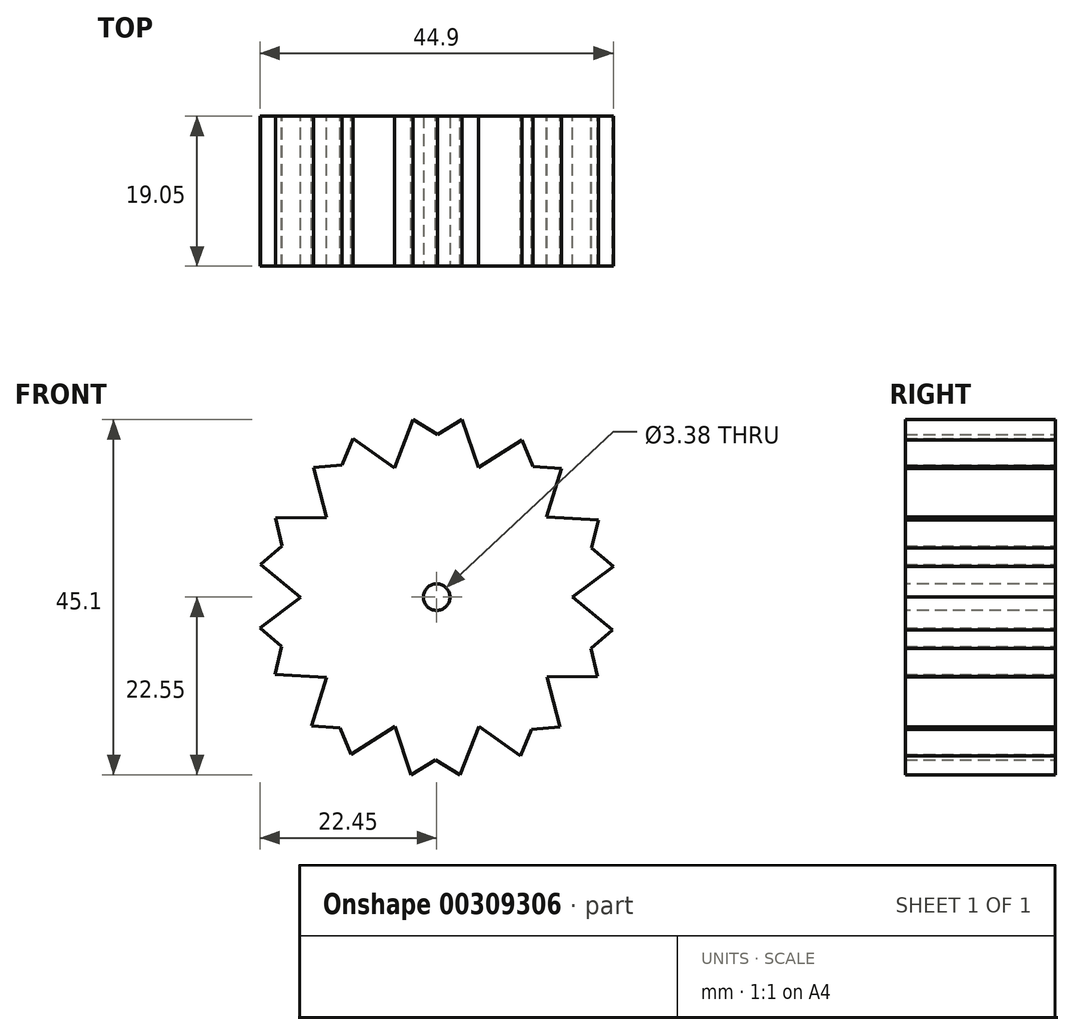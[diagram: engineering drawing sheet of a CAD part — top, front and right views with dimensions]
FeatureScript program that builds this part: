
annotation { "Feature Type Name" : "Feature", "Feature Type Description" : "" }
export const myFeature = defineFeature(function(context is Context, id is Id, definition is map)
    precondition{}
    {
        {
            var Q0;
            Q0=qCreatedBy(makeId("Front.planeOp"),FACE);
            var sketch = newSketch(context, id + "F0", { "sketchPlane" : qUnion([Q0])});
            skCircle(sketch, "E0", {"center": v(0, 0) * mm, "radius": 15.81 * mm});
            skLineSegment(sketch, "E1", {"start": v(-6.47, 13.66) * mm, "end": v(-2.97, 22.55) * mm});
            skLineSegment(sketch, "E2", {"start": v(-2.97, 22.55) * mm, "end": v(0.14, 20.66) * mm});
            skLineSegment(sketch, "E3", {"start": v(0.14, 20.66) * mm, "end": v(3.25, 22.55) * mm});
            skLineSegment(sketch, "E4", {"start": v(3.25, 22.55) * mm, "end": v(5.95, 14.5) * mm});
            skLineSegment(sketch, "E5.1.0", {"start": v(-15.66, 16.5) * mm, "end": v(-12.03, 16.8) * mm});
            skLineSegment(sketch, "E5.1.1", {"start": v(-12.03, 16.8) * mm, "end": v(-10.63, 20.15) * mm});
            skLineSegment(sketch, "E5.1.2", {"start": v(-10.63, 20.15) * mm, "end": v(-3.7, 15.23) * mm});
            skLineSegment(sketch, "E5.1.3", {"start": v(-13.26, 7.25) * mm, "end": v(-15.66, 16.5) * mm});
            skLineSegment(sketch, "E5.2.0", {"start": v(-22.36, 4.14) * mm, "end": v(-19.6, 6.52) * mm});
            skLineSegment(sketch, "E5.2.1", {"start": v(-19.6, 6.52) * mm, "end": v(-20.44, 10.05) * mm});
            skLineSegment(sketch, "E5.2.2", {"start": v(-20.44, 10.05) * mm, "end": v(-11.95, 10.14) * mm});
            skLineSegment(sketch, "E5.2.3", {"start": v(-15, -1.93) * mm, "end": v(-22.36, 4.14) * mm});
            skLineSegment(sketch, "E5.3.0", {"start": v(-20.52, -9.8) * mm, "end": v(-19.7, -6.25) * mm});
            skLineSegment(sketch, "E5.3.1", {"start": v(-19.7, -6.25) * mm, "end": v(-22.45, -3.88) * mm});
            skLineSegment(sketch, "E5.3.2", {"start": v(-22.45, -3.88) * mm, "end": v(-15.63, 1.18) * mm});
            skLineSegment(sketch, "E5.3.3", {"start": v(-11, -10.37) * mm, "end": v(-20.52, -9.8) * mm});
            skLineSegment(sketch, "E5.4.0", {"start": v(-10.85, -19.99) * mm, "end": v(-12.26, -16.63) * mm});
            skLineSegment(sketch, "E5.4.1", {"start": v(-12.26, -16.63) * mm, "end": v(-15.88, -16.33) * mm});
            skLineSegment(sketch, "E5.4.2", {"start": v(-15.88, -16.33) * mm, "end": v(-13.34, -8.23) * mm});
            skLineSegment(sketch, "E5.4.3", {"start": v(-2.8, -14.86) * mm, "end": v(-10.85, -19.99) * mm});
            skLineSegment(sketch, "E5.5.0", {"start": v(2.97, -22.55) * mm, "end": v(-0.14, -20.66) * mm});
            skLineSegment(sketch, "E5.5.1", {"start": v(-0.14, -20.66) * mm, "end": v(-3.25, -22.55) * mm});
            skLineSegment(sketch, "E5.5.2", {"start": v(-3.25, -22.55) * mm, "end": v(-5.95, -14.5) * mm});
            skLineSegment(sketch, "E5.5.3", {"start": v(6.47, -13.66) * mm, "end": v(2.97, -22.55) * mm});
            skLineSegment(sketch, "E5.6.0", {"start": v(15.66, -16.5) * mm, "end": v(12.03, -16.8) * mm});
            skLineSegment(sketch, "E5.6.1", {"start": v(12.03, -16.8) * mm, "end": v(10.63, -20.15) * mm});
            skLineSegment(sketch, "E5.6.2", {"start": v(10.63, -20.15) * mm, "end": v(3.7, -15.23) * mm});
            skLineSegment(sketch, "E5.6.3", {"start": v(13.26, -7.25) * mm, "end": v(15.66, -16.5) * mm});
            skLineSegment(sketch, "E5.7.0", {"start": v(22.36, -4.14) * mm, "end": v(19.6, -6.52) * mm});
            skLineSegment(sketch, "E5.7.1", {"start": v(19.6, -6.52) * mm, "end": v(20.44, -10.05) * mm});
            skLineSegment(sketch, "E5.7.2", {"start": v(20.44, -10.05) * mm, "end": v(11.95, -10.14) * mm});
            skLineSegment(sketch, "E5.7.3", {"start": v(15, 1.93) * mm, "end": v(22.36, -4.14) * mm});
            skLineSegment(sketch, "E5.8.0", {"start": v(20.52, 9.8) * mm, "end": v(19.7, 6.25) * mm});
            skLineSegment(sketch, "E5.8.1", {"start": v(19.7, 6.25) * mm, "end": v(22.45, 3.88) * mm});
            skLineSegment(sketch, "E5.8.2", {"start": v(22.45, 3.88) * mm, "end": v(15.63, -1.18) * mm});
            skLineSegment(sketch, "E5.8.3", {"start": v(11, 10.37) * mm, "end": v(20.52, 9.8) * mm});
            skLineSegment(sketch, "E5.9.0", {"start": v(10.85, 19.99) * mm, "end": v(12.26, 16.63) * mm});
            skLineSegment(sketch, "E5.9.1", {"start": v(12.26, 16.63) * mm, "end": v(15.88, 16.33) * mm});
            skLineSegment(sketch, "E5.9.2", {"start": v(15.88, 16.33) * mm, "end": v(13.34, 8.23) * mm});
            skLineSegment(sketch, "E5.9.3", {"start": v(2.8, 14.86) * mm, "end": v(10.85, 19.99) * mm});
            skSolve(sketch);
        }
        {
            var Q0;
            Q0=makeQuery(id+"F0.imprint","IMPRINT",FACE,{"disambiguationData":[TD([[makeQuery(id+"F0.imprint","IMPRINT",EDGE,{"derivedFrom":sQuery(id+"F0.wireOp",EDGE,"E0")}),1.0]])]});
            extrude(context, id + "F1", {"entities" : qUnion([Q0]), "depth" : 19.05 * mm});
        }
        {
            var Q0;
            Q0=makeQuery(id+"F1.opExtrude","CAP_FACE",FACE,{"disambiguationData":[OSD([sQuery(id+"F0.wireOp",EDGE,"E0")])],"isStart":false});
            var sketch = newSketch(context, id + "F2", { "sketchPlane" : qUnion([Q0])});
            skCircle(sketch, "E6", {"center": v(0, 0) * mm, "radius": 1.69 * mm});
            skSolve(sketch);
        }
        {
            var Q0;
            Q0=makeQuery(id+"F2.imprint","IMPRINT",FACE,{"disambiguationData":[TD([[makeQuery(id+"F2.imprint","IMPRINT",EDGE,{"derivedFrom":sQuery(id+"F2.wireOp",EDGE,"E6")}),1.0]])]});
            extrude(context, id + "F3", {"entities" : qUnion([Q0]), "operationType" : NewBodyOperationType.REMOVE, "oppositeDirection" : true, "depth" : 19.05 * mm});
        }
        {
            var Q0;
            Q0 = qSketchRegion(id + "F0", true);
            extrude(context, id + "F4", {"entities" : qUnion([Q0]), "operationType" : NewBodyOperationType.ADD, "depth" : 19.05 * mm});
        }
    });
